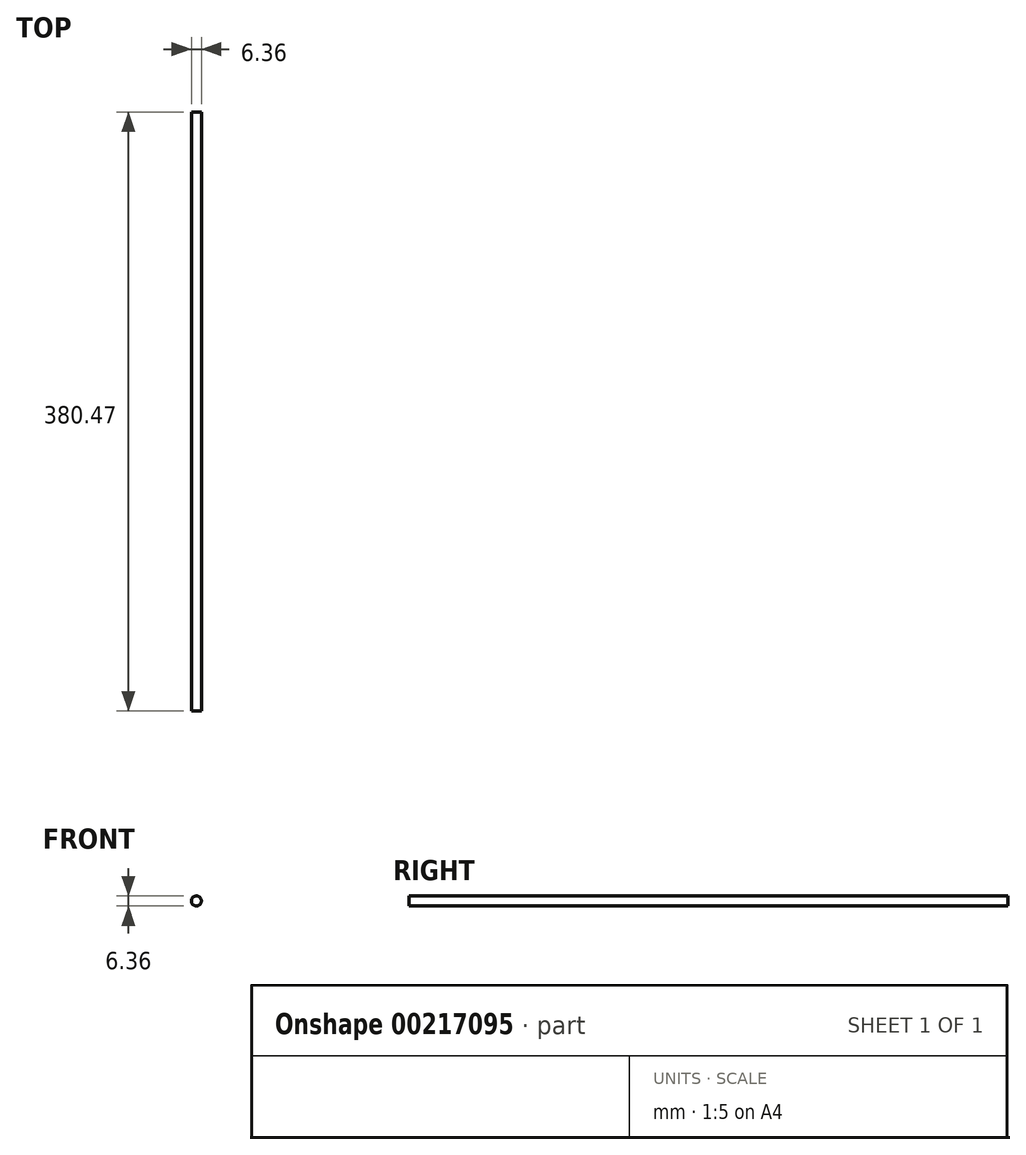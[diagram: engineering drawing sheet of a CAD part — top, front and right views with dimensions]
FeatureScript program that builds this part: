
annotation { "Feature Type Name" : "Feature", "Feature Type Description" : "" }
export const myFeature = defineFeature(function(context is Context, id is Id, definition is map)
    precondition{}
    {
        {
            var Q0;
            Q0=qCreatedBy(makeId("Front.planeOp"),FACE);
            var sketch = newSketch(context, id + "F0", { "sketchPlane" : qUnion([Q0])});
            skCircle(sketch, "E0", {"center": v(0, 0) * mm, "radius": 3.18 * mm});
            skSolve(sketch);
        }
        {
            var Q0;
            Q0 = qSketchRegion(id + "F0", true);
            extrude(context, id + "F1", {"entities" : qUnion([Q0]), "depth" : 380.47 * mm});
        }
    });
